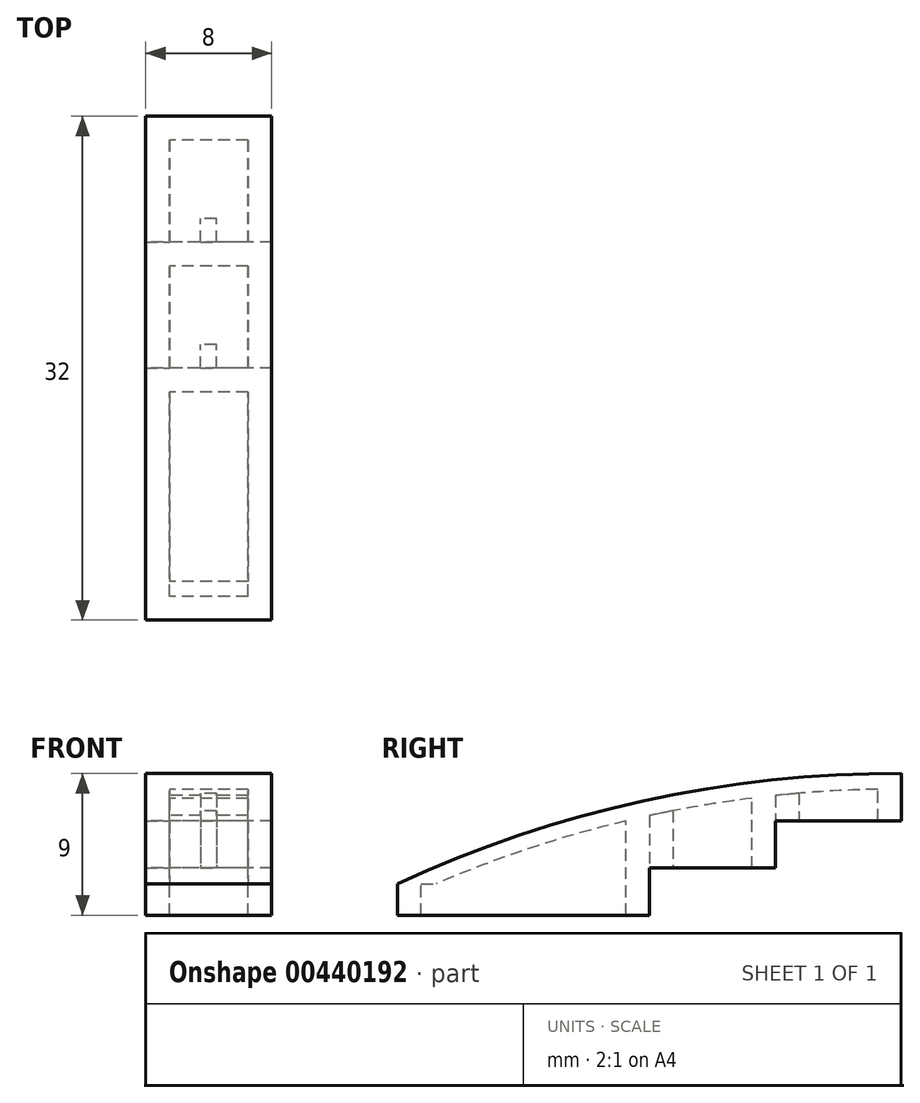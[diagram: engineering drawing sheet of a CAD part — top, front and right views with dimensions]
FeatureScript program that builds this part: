
annotation { "Feature Type Name" : "Feature", "Feature Type Description" : "" }
export const myFeature = defineFeature(function(context is Context, id is Id, definition is map)
    precondition{}
    {
        {
            var Q0;
            Q0=qCreatedBy(makeId("Right.planeOp"),FACE);
            var sketch = newSketch(context, id + "F0", { "sketchPlane" : qUnion([Q0])});
            skLineSegment(sketch, "E0.bottom", {"start": v(0, 0) * mm, "end": v(16, 0) * mm});
            skLineSegment(sketch, "E0.left", {"start": v(0, 0) * mm, "end": v(0, 2) * mm});
            skLineSegment(sketch, "E0.right", {"start": v(32, 6) * mm, "end": v(32, 9) * mm});
            skArc(sketch, "E1", {"start": v(32, 9) * mm, "mid": v(15.61, 7.27) * mm, "end": v(0, 2) * mm});
            skLineSegment(sketch, "E2", {"start": v(16, 0) * mm, "end": v(16, 6.33) * mm});
            skLineSegment(sketch, "E3", {"start": v(16, 3) * mm, "end": v(24, 3) * mm});
            skLineSegment(sketch, "E4", {"start": v(24, 3) * mm, "end": v(24, 7.6) * mm});
            skLineSegment(sketch, "E5", {"start": v(24, 6) * mm, "end": v(32, 6) * mm});
            skArc(sketch, "E6.0", {"start": v(30.5, 8) * mm, "mid": v(27.25, 7.87) * mm, "end": v(24, 7.6) * mm});
            skLineSegment(sketch, "E7.0", {"start": v(1.5, 0) * mm, "end": v(1.5, 1.58) * mm});
            skLineSegment(sketch, "E8.0", {"start": v(22.5, 3) * mm, "end": v(22.5, 7.43) * mm});
            skLineSegment(sketch, "E9", {"start": v(30.5, 6) * mm, "end": v(30.5, 8) * mm});
            skLineSegment(sketch, "E10", {"start": v(14.5, 0) * mm, "end": v(14.5, 5.99) * mm});
            skArc(sketch, "E11.trimOffspring", {"start": v(14.5, 5.99) * mm, "mid": v(7.9, 4.09) * mm, "end": v(1.5, 1.58) * mm});
            skArc(sketch, "E12.trimOffspring", {"start": v(22.5, 7.43) * mm, "mid": v(19.24, 6.95) * mm, "end": v(16, 6.33) * mm});
            skSolve(sketch);
        }
        {
            var Q0;
            {var subQ12=sQuery(id+"F0.wireOp",EDGE,"E0.left");Q0=makeQuery(id+"F0.imprint","IMPRINT",FACE,{"disambiguationData":[TD([[makeQuery(id+"F0.imprint","IMPRINT",EDGE,{"derivedFrom":subQ12}),-1.0]])]});}
            var Q1;
            {var subQ0=sQuery(id+"F0.wireOp",EDGE,"E7.0");Q1=makeQuery(id+"F0.imprint","IMPRINT",FACE,{"disambiguationData":[TD([[makeQuery(id+"F0.imprint","IMPRINT",EDGE,{"derivedFrom":subQ0}),-1.0]])]});}
            var Q2;
            {var subQ4=sQuery(id+"F0.wireOp",EDGE,"E8.0");Q2=makeQuery(id+"F0.imprint","IMPRINT",FACE,{"disambiguationData":[TD([[makeQuery(id+"F0.imprint","IMPRINT",EDGE,{"derivedFrom":subQ4}),1.0]])]});}
            var Q3;
            {var subQ0=sQuery(id+"F0.wireOp",EDGE,"E6.0");Q3=makeQuery(id+"F0.imprint","IMPRINT",FACE,{"disambiguationData":[TD([[makeQuery(id+"F0.imprint","IMPRINT",EDGE,{"derivedFrom":subQ0}),1.0]])]});}
            extrude(context, id + "F1", {"entities" : qUnion([Q0, Q1, Q2, Q3]), "depth" : 4 * mm});
        }
        {
            var Q0;
            {var subQ0=sQuery(id+"F0.wireOp",EDGE,"E6.0");Q0=makeQuery(id+"F0.imprint","IMPRINT",FACE,{"disambiguationData":[TD([[makeQuery(id+"F0.imprint","IMPRINT",EDGE,{"derivedFrom":subQ0}),1.0]])]});}
            var Q1;
            {var subQ4=sQuery(id+"F0.wireOp",EDGE,"E8.0");Q1=makeQuery(id+"F0.imprint","IMPRINT",FACE,{"disambiguationData":[TD([[makeQuery(id+"F0.imprint","IMPRINT",EDGE,{"derivedFrom":subQ4}),1.0]])]});}
            var Q2;
            {var subQ0=sQuery(id+"F0.wireOp",EDGE,"E7.0");Q2=makeQuery(id+"F0.imprint","IMPRINT",FACE,{"disambiguationData":[TD([[makeQuery(id+"F0.imprint","IMPRINT",EDGE,{"derivedFrom":subQ0}),-1.0]])]});}
            extrude(context, id + "F2", {"entities" : qUnion([Q0, Q1, Q2]), "operationType" : NewBodyOperationType.REMOVE, "depth" : 2.5 * mm});
        }
        {
            var Q0;
            Q0=makeQuery(id+"F1.opExtrude","SWEPT_BODY",BODY,{"disambiguationData":[OSD([sQuery(id+"F0.wireOp",EDGE,"E0.bottom"),sQuery(id+"F0.wireOp",EDGE,"E0.left"),sQuery(id+"F0.wireOp",EDGE,"E0.right"),sQuery(id+"F0.wireOp",EDGE,"E1"),sQuery(id+"F0.wireOp",EDGE,"E2"),sQuery(id+"F0.wireOp",EDGE,"E3"),sQuery(id+"F0.wireOp",EDGE,"E4"),sQuery(id+"F0.wireOp",EDGE,"E5")])]});
            var Q1;
            Q1=makeQuery(id+"F1.opExtrude","CAP_FACE",FACE,{"disambiguationData":[OSD([sQuery(id+"F0.wireOp",EDGE,"E0.bottom"),sQuery(id+"F0.wireOp",EDGE,"E0.left"),sQuery(id+"F0.wireOp",EDGE,"E0.right"),sQuery(id+"F0.wireOp",EDGE,"E1"),sQuery(id+"F0.wireOp",EDGE,"E2"),sQuery(id+"F0.wireOp",EDGE,"E3"),sQuery(id+"F0.wireOp",EDGE,"E4"),sQuery(id+"F0.wireOp",EDGE,"E5")])],"isStart":true});
            mirror(context, id + "F3", {"operationType" : NewBodyOperationType.ADD, "entities" : qUnion([Q0]), "mirrorPlane" : qUnion([Q1])});
        }
        {
            var Q0;
            {var subQ0=makeQuery(id+"F1.opExtrude","SWEPT_FACE",FACE,{"disambiguationData":[OSD([sQuery(id+"F0.wireOp",EDGE,"E5")])]});Q0=makeQuery(id+"F3.boolean.opBoolean","MERGE",FACE,{"derivedFrom":[subQ0,makeQuery(id+"F3.opPattern","COPY",FACE,{"derivedFrom":subQ0,"instanceName":"1"})]});}
            var sketch = newSketch(context, id + "F4", { "sketchPlane" : qUnion([Q0])});
            skLineSegment(sketch, "E13.bottom", {"start": v(-0.5, -24) * mm, "end": v(0.5, -24) * mm});
            skLineSegment(sketch, "E13.top", {"start": v(-0.5, -25.5) * mm, "end": v(0.5, -25.5) * mm});
            skLineSegment(sketch, "E13.left", {"start": v(-0.5, -24) * mm, "end": v(-0.5, -25.5) * mm});
            skLineSegment(sketch, "E13.right", {"start": v(0.5, -24) * mm, "end": v(0.5, -25.5) * mm});
            skSolve(sketch);
        }
        {
            var Q0;
            Q0=qSketchRegion(id+"F4",true);
            extrude(context, id + "F5", {"entities" : qUnion([Q0]), "operationType" : NewBodyOperationType.ADD, "endBound" : BoundingType.UP_TO_NEXT, "oppositeDirection" : true, "depth" : 25 * mm});
        }
        {
            var Q0;
            {var subQ0=makeQuery(id+"F1.opExtrude","SWEPT_FACE",FACE,{"disambiguationData":[OSD([sQuery(id+"F0.wireOp",EDGE,"E3")])]});Q0=makeQuery(id+"F3.boolean.opBoolean","MERGE",FACE,{"derivedFrom":[subQ0,makeQuery(id+"F3.opPattern","COPY",FACE,{"derivedFrom":subQ0,"instanceName":"1"})]});}
            var sketch = newSketch(context, id + "F6", { "sketchPlane" : qUnion([Q0])});
            skLineSegment(sketch, "E14.bottom", {"start": v(-0.5, -16) * mm, "end": v(0.5, -16) * mm});
            skLineSegment(sketch, "E14.top", {"start": v(-0.5, -17.5) * mm, "end": v(0.5, -17.5) * mm});
            skLineSegment(sketch, "E14.left", {"start": v(-0.5, -16) * mm, "end": v(-0.5, -17.5) * mm});
            skLineSegment(sketch, "E14.right", {"start": v(0.5, -16) * mm, "end": v(0.5, -17.5) * mm});
            skSolve(sketch);
        }
        {
            var Q0;
            Q0=qSketchRegion(id+"F6",true);
            extrude(context, id + "F7", {"entities" : qUnion([Q0]), "operationType" : NewBodyOperationType.ADD, "endBound" : BoundingType.UP_TO_NEXT, "oppositeDirection" : true, "depth" : 25 * mm});
        }
        {
            var Q0;
            {var subQ0=makeQuery(id+"F1.opExtrude","SWEPT_FACE",FACE,{"disambiguationData":[OSD([sQuery(id+"F0.wireOp",EDGE,"E0.bottom")])]});Q0=makeQuery(id+"F3.boolean.opBoolean","MERGE",FACE,{"derivedFrom":[subQ0,makeQuery(id+"F3.opPattern","COPY",FACE,{"derivedFrom":subQ0,"instanceName":"1"})]});}
            var sketch = newSketch(context, id + "F8", { "sketchPlane" : qUnion([Q0])});
            skLineSegment(sketch, "E15.bottom", {"start": v(-2.5, -1.5) * mm, "end": v(2.5, -1.5) * mm});
            skLineSegment(sketch, "E15.top", {"start": v(-2.5, -6.5) * mm, "end": v(2.5, -6.5) * mm});
            skLineSegment(sketch, "E15.left", {"start": v(-2.5, -1.5) * mm, "end": v(-2.5, -6.5) * mm});
            skLineSegment(sketch, "E15.right", {"start": v(2.5, -1.5) * mm, "end": v(2.5, -6.5) * mm});
            skSolve(sketch);
        }
        {
            var Q0;
            Q0=qSketchRegion(id+"F8",true);
            extrude(context, id + "F9", {"entities" : qUnion([Q0]), "operationType" : NewBodyOperationType.REMOVE, "oppositeDirection" : true, "depth" : 2 * mm});
        }
    });
